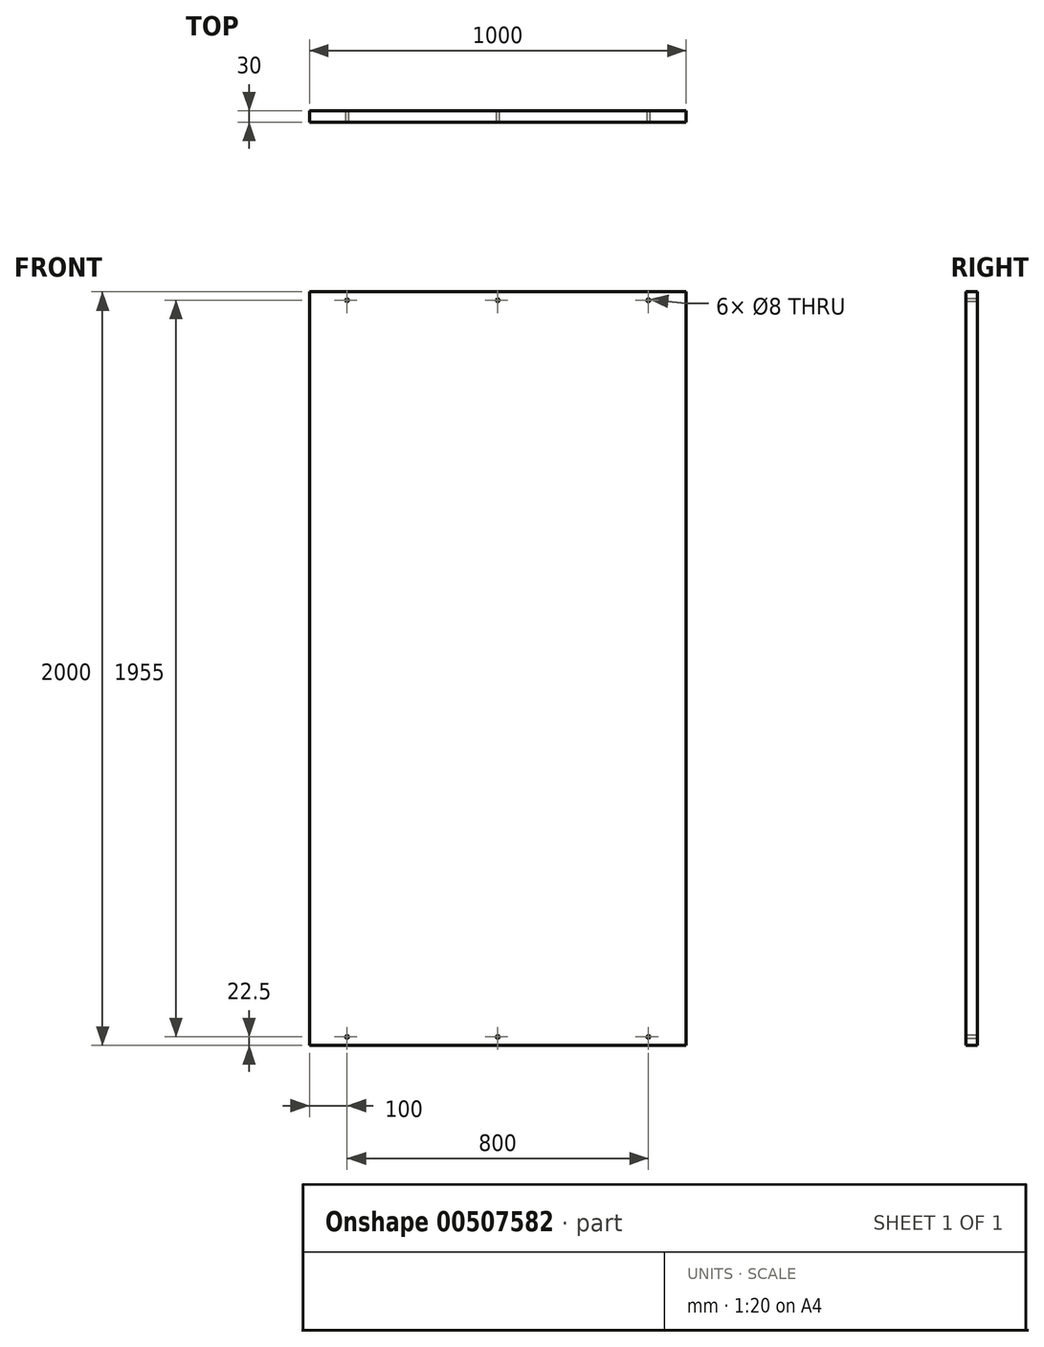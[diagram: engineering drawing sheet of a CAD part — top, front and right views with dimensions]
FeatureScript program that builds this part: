
annotation { "Feature Type Name" : "Feature", "Feature Type Description" : "" }
export const myFeature = defineFeature(function(context is Context, id is Id, definition is map)
    precondition{}
    {
        {
            var Q0;
            Q0=qCreatedBy(makeId("Front.planeOp"),FACE);
            var sketch = newSketch(context, id + "F0", { "sketchPlane" : qUnion([Q0])});
            skLineSegment(sketch, "E0.bottom", {"start": v(0, 0) * mm, "end": v(1000, 0) * mm});
            skLineSegment(sketch, "E0.top", {"start": v(0, 2000) * mm, "end": v(1000, 2000) * mm});
            skLineSegment(sketch, "E0.left", {"start": v(0, 0) * mm, "end": v(0, 2000) * mm});
            skLineSegment(sketch, "E0.right", {"start": v(1000, 0) * mm, "end": v(1000, 2000) * mm});
            skSolve(sketch);
        }
        {
            var Q0;
            Q0=makeQuery(id+"F0.imprint","IMPRINT",FACE,{"disambiguationData":[TD([[makeQuery(id+"F0.imprint","IMPRINT",EDGE,{"derivedFrom":sQuery(id+"F0.wireOp",EDGE,"E0.bottom")}),1.0]])]});
            extrude(context, id + "F1", {"entities" : qUnion([Q0]), "depth" : 30 * mm, "offsetDistance" : 25 * mm});
        }
        {
            var Q0;
            Q0=makeQuery(id+"F1.opExtrude","CAP_FACE",FACE,{"disambiguationData":[OSD([sQuery(id+"F0.wireOp",EDGE,"E0.bottom"),sQuery(id+"F0.wireOp",EDGE,"E0.top"),sQuery(id+"F0.wireOp",EDGE,"E0.left"),sQuery(id+"F0.wireOp",EDGE,"E0.right")])],"isStart":false});
            var sketch = newSketch(context, id + "F2", { "sketchPlane" : qUnion([Q0])});
            skLineSegment(sketch, "E1.bottom", {"start": v(0, 0) * mm, "end": v(1000, 0) * mm});
            skLineSegment(sketch, "E1.top", {"start": v(0, 90) * mm, "end": v(1000, 90) * mm});
            skLineSegment(sketch, "E1.left", {"start": v(0, 0) * mm, "end": v(0, 90) * mm});
            skLineSegment(sketch, "E1.right", {"start": v(1000, 0) * mm, "end": v(1000, 90) * mm});
            skLineSegment(sketch, "E2.bottom", {"start": v(0, 2000) * mm, "end": v(1000, 2000) * mm});
            skLineSegment(sketch, "E2.top", {"start": v(0, 1910) * mm, "end": v(1000, 1910) * mm});
            skLineSegment(sketch, "E2.left", {"start": v(0, 2000) * mm, "end": v(0, 1910) * mm});
            skLineSegment(sketch, "E2.right", {"start": v(1000, 2000) * mm, "end": v(1000, 1910) * mm});
            skCircle(sketch, "E3", {"center": v(100, 1977.5) * mm, "radius": 4 * mm});
            skCircle(sketch, "E4", {"center": v(500, 1977.5) * mm, "radius": 4 * mm});
            skCircle(sketch, "E5", {"center": v(900, 1977.5) * mm, "radius": 4 * mm});
            skPoint(sketch, "E5.centerSnap0", {"position": v(1000, 1955) * mm});
            skCircle(sketch, "E6", {"center": v(100, 22.5) * mm, "radius": 4 * mm});
            skCircle(sketch, "E7", {"center": v(500, 22.5) * mm, "radius": 4 * mm});
            skCircle(sketch, "E8", {"center": v(900, 22.5) * mm, "radius": 4 * mm});
            skSolve(sketch);
        }
        {
            var Q0;
            Q0=makeQuery(id+"F2.imprint","IMPRINT",FACE,{"disambiguationData":[TD([[makeQuery(id+"F2.imprint","IMPRINT",EDGE,{"derivedFrom":sQuery(id+"F2.wireOp",EDGE,"E6")}),1.0]])]});
            var Q1;
            Q1=makeQuery(id+"F2.imprint","IMPRINT",FACE,{"disambiguationData":[TD([[makeQuery(id+"F2.imprint","IMPRINT",EDGE,{"derivedFrom":sQuery(id+"F2.wireOp",EDGE,"E7")}),1.0]])]});
            var Q2;
            Q2=makeQuery(id+"F2.imprint","IMPRINT",FACE,{"disambiguationData":[TD([[makeQuery(id+"F2.imprint","IMPRINT",EDGE,{"derivedFrom":sQuery(id+"F2.wireOp",EDGE,"E8")}),1.0]])]});
            var Q3;
            Q3=makeQuery(id+"F2.imprint","IMPRINT",FACE,{"disambiguationData":[TD([[makeQuery(id+"F2.imprint","IMPRINT",EDGE,{"derivedFrom":sQuery(id+"F2.wireOp",EDGE,"E3")}),1.0]])]});
            var Q4;
            Q4=makeQuery(id+"F2.imprint","IMPRINT",FACE,{"disambiguationData":[TD([[makeQuery(id+"F2.imprint","IMPRINT",EDGE,{"derivedFrom":sQuery(id+"F2.wireOp",EDGE,"E4")}),1.0]])]});
            var Q5;
            Q5=makeQuery(id+"F2.imprint","IMPRINT",FACE,{"disambiguationData":[TD([[makeQuery(id+"F2.imprint","IMPRINT",EDGE,{"derivedFrom":sQuery(id+"F2.wireOp",EDGE,"E5")}),1.0]])]});
            extrude(context, id + "F3", {"entities" : qUnion([Q0, Q1, Q2, Q3, Q4, Q5]), "operationType" : NewBodyOperationType.REMOVE, "oppositeDirection" : true, "depth" : 30 * mm, "offsetDistance" : 25 * mm});
        }
    });
